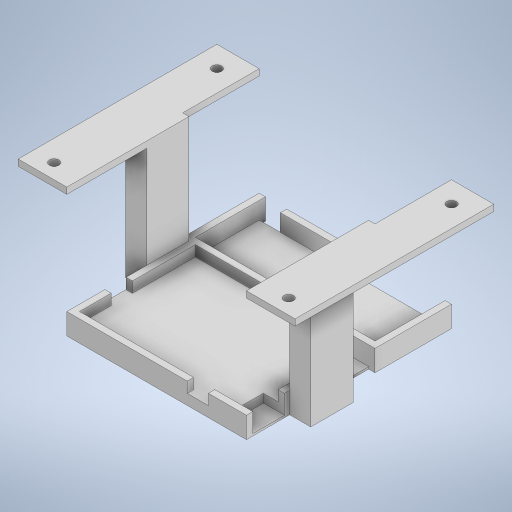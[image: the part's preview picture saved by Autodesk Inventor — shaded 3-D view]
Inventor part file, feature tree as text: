
AUTODESK INVENTOR PART (.ipt)
format: ipt  version: 2023 (Build 270158000, 158)  size: 402,944 bytes
history: native  units: mm
features: extrude x9, sketch x9, other x1
ambient origin geometry x8: Origin, YZ Plane, XZ Plane, XY Plane, X Axis, Y Axis, Z Axis, Center Point
bodies: Body1 (feature_tree)
feature tree (19):
  other  "Sólido1"
  extrude  "Extrusión1"  Depth=10.0mm TaperAngle=0.0deg
  extrude  "Extrusión2"  Depth=5.0mm TaperAngle=0.0deg
  extrude  "Extrusión3"  Depth=10.0mm TaperAngle=0.0deg
  extrude  "Extrusión4"  Depth=30.0mm
  extrude  "Extrusión5"  Depth=10.0mm
  extrude  "Extrusión6"  TaperAngle=0.0deg  [1 undecoded]
  extrude  "Extrusión7"  Depth=10.0mm TaperAngle=0.0deg
  extrude  "Extrusión8"  Depth=18.0mm
  extrude  "Extrusión9"  TaperAngle=0.0deg  [1 undecoded]
  sketch  "Boceto1"  dims[d0=79.0mm d1=85.0mm d2=3.0mm d3=10.0mm d4=0.0mm]
  sketch  "Boceto2"  dims[d8=3.0mm d9=85.0mm d10=79.0mm d11=30.0mm d12=57.8mm d13=5.0mm d14=0.0mm]
  sketch  "Boceto3"  dims[d15=3.0mm d16=30.0mm d17=10.0mm d18=0.0mm]
  sketch  "Boceto4"  dims[d19=8.0mm d20=0.0mm d21=30.0mm]
  sketch  "Boceto5"  dims[d24=10.0mm d25=10.0mm]
  sketch  "Boceto6"  dims[d27=15.0mm d28=0.0mm]
  sketch  "Boceto7"  dims[d29=0.0mm d30=10.0mm d31=0.0mm]
  sketch  "Boceto8"  dims[d32=10.0mm d33=18.0mm]
  sketch  "Boceto9"  dims[d34=0.0mm d35=0.0mm d36=10.0mm d37=0.0mm d41=15.0mm d42=9.0mm d43=0.0mm d44=10.0mm d45=0.0mm d46=15.0mm d47=9.0mm d48=10.0mm d49=20.0mm d50=0.0mm d51=10.0mm d52=20.0mm d53=2.4mm d54=2.4mm d55=58.0mm d56=0.0mm d57=20.0mm d58=4.5mm d59=10.0mm d60=10.0mm d61=3.0mm d62=0.0mm]
note: 2 required parameter values undecoded (feature->parameter linkage not recoverable at this tier; creation-order binding heuristic only, values carry confidence <= 0.55)
